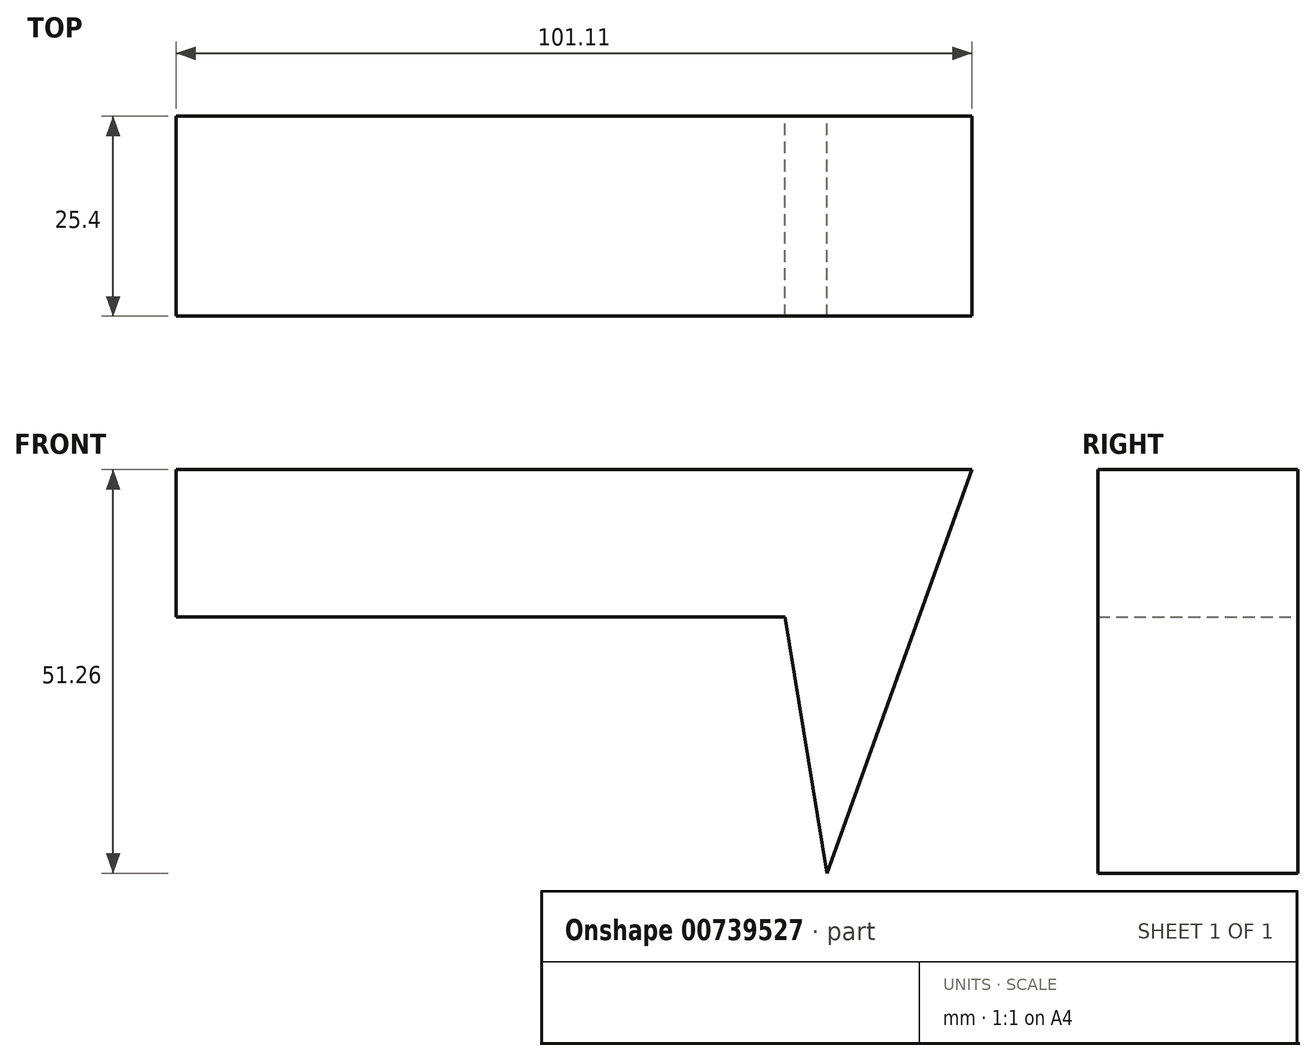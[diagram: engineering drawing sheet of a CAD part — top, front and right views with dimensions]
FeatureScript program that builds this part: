
annotation { "Feature Type Name" : "Feature", "Feature Type Description" : "" }
export const myFeature = defineFeature(function(context is Context, id is Id, definition is map)
    precondition{}
    {
        {
            var Q0;
            Q0=qCreatedBy(makeId("Front.planeOp"),FACE);
            var sketch = newSketch(context, id + "F0", { "sketchPlane" : qUnion([Q0])});
            skLineSegment(sketch, "E0", {"start": v(0, 0) * mm, "end": v(-5.38, 32.57) * mm});
            skLineSegment(sketch, "E1", {"start": v(-5.38, 32.57) * mm, "end": v(-82.7, 32.57) * mm});
            skLineSegment(sketch, "E2", {"start": v(-82.7, 32.57) * mm, "end": v(-82.7, 51.26) * mm});
            skLineSegment(sketch, "E3", {"start": v(-82.7, 51.26) * mm, "end": v(18.4, 51.26) * mm});
            skLineSegment(sketch, "E4", {"start": v(18.4, 51.26) * mm, "end": v(0, 0) * mm});
            skSolve(sketch);
        }
        {
            var Q0;
            Q0 = qSketchRegion(id + "F0", true);
            extrude(context, id + "F1", {"entities" : qUnion([Q0]), "depth" : 25.4 * mm, "offsetDistance" : 25.4 * mm});
        }
    });
